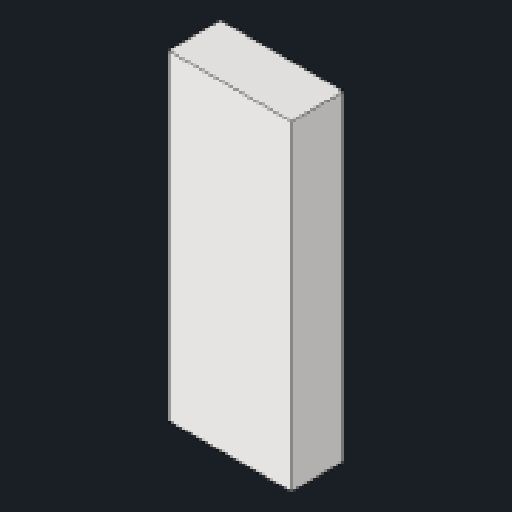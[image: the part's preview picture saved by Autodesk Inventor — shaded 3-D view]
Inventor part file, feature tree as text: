
AUTODESK INVENTOR PART (.ipt)
format: ipt  version: 2023.2 (Build 272271030, 271C)  size: 78,336 bytes
history: native  units: mm
features: extrude x1, sketch x1
ambient origin geometry x8: Origin, YZ Plane, XZ Plane, XY Plane, X Axis, Y Axis, Z Axis, Center Point
bodies: Solid1 (feature_tree)
feature tree (2):
  extrude  "Extrusion1"  Depth=52.0mm
  sketch  "Sketch1"  dims[d0=20.0mm d1=52.0mm d2=8.5mm d3=0.0mm]
